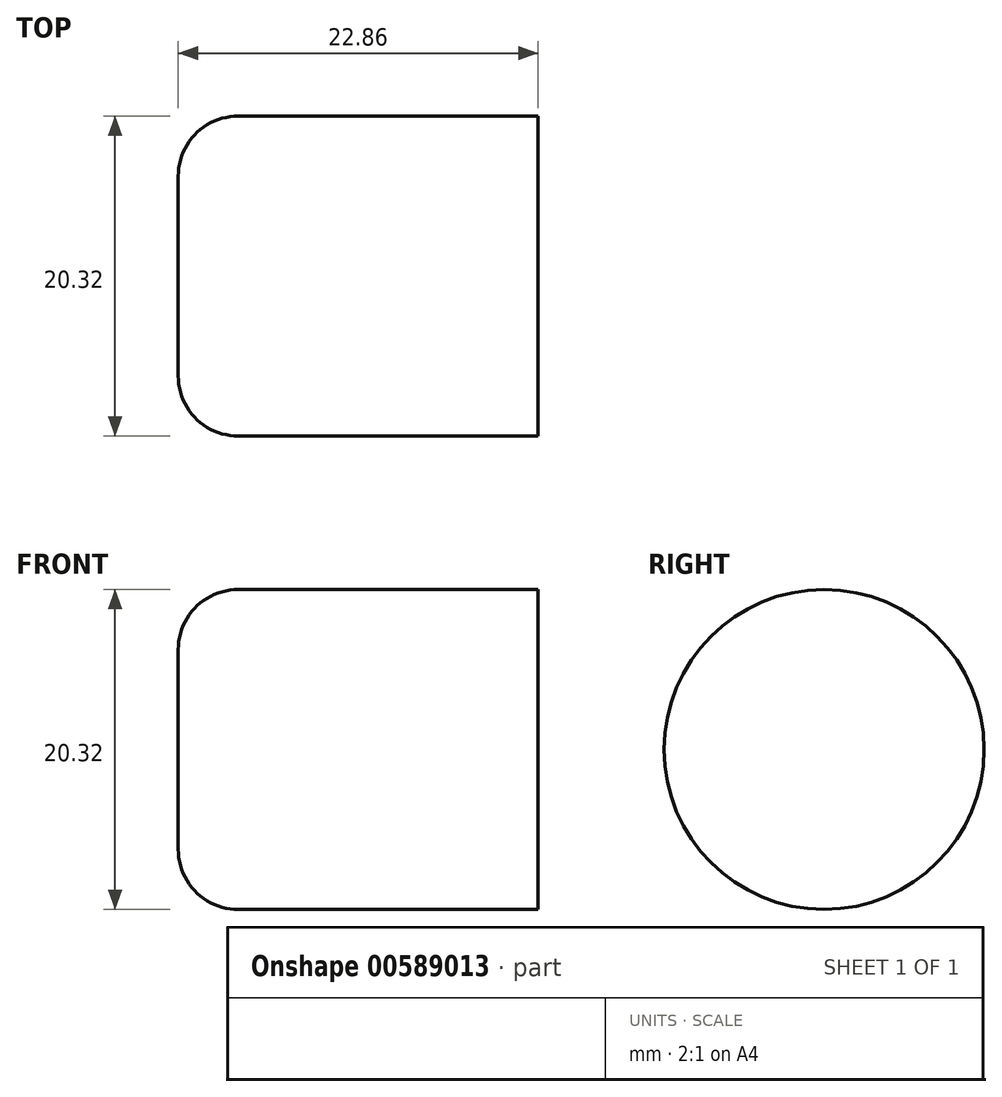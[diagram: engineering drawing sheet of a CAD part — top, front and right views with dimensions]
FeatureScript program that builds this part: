
annotation { "Feature Type Name" : "Feature", "Feature Type Description" : "" }
export const myFeature = defineFeature(function(context is Context, id is Id, definition is map)
    precondition{}
    {
        {
            var Q0;
            Q0=qCreatedBy(makeId("Top.planeOp"),FACE);
            var sketch = newSketch(context, id + "F0", { "sketchPlane" : qUnion([Q0])});
            skLineSegment(sketch, "E0", {"start": v(0, 0) * mm, "end": v(22.86, 0) * mm});
            skLineSegment(sketch, "E1", {"start": v(22.86, 0) * mm, "end": v(22.86, 10.16) * mm});
            skLineSegment(sketch, "E2", {"start": v(22.86, 10.16) * mm, "end": v(3.81, 10.16) * mm});
            skLineSegment(sketch, "E3", {"start": v(0, 6.35) * mm, "end": v(0, 0) * mm});
            skPoint(sketch, "E4.visualSharp", {"position": v(0, 10.16) * mm});
            skArc(sketch, "E4.filletArc", {"start": v(3.8, 10.16) * mm, "mid": v(1.12, 9.04) * mm, "end": v(0, 6.35) * mm});
            skSolve(sketch);
        }
        {
            var Q0;
            Q0 = qSketchRegion(id + "F0", true);
            var Q1;
            Q1=sQuery(id+"F0.wireOp",EDGE,"E0");
            revolve(context, id + "F1", {"entities" : qUnion([Q0]), "axis" : qUnion([Q1]), "revolveType" : RevolveType.FULL});
        }
    });
